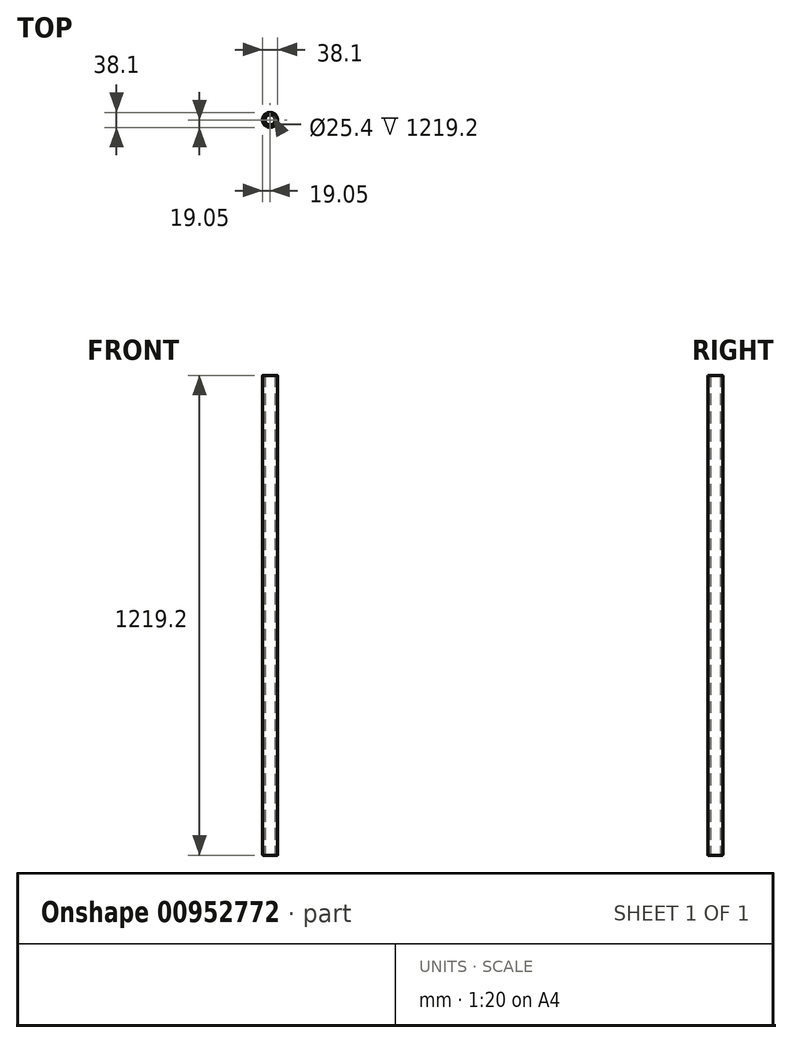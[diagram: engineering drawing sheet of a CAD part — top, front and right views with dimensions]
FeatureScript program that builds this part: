
annotation { "Feature Type Name" : "Feature", "Feature Type Description" : "" }
export const myFeature = defineFeature(function(context is Context, id is Id, definition is map)
    precondition{}
    {
        {
            var Q0;
            Q0=qCreatedBy(makeId("Top.planeOp"),FACE);
            var sketch = newSketch(context, id + "F0", { "sketchPlane" : qUnion([Q0])});
            skCircle(sketch, "E0", {"center": v(0, 0) * mm, "radius": 19.05 * mm});
            skCircle(sketch, "E1", {"center": v(0, 0) * mm, "radius": 12.7 * mm});
            skSolve(sketch);
        }
        {
            var Q0;
            Q0 = qSketchRegion(id + "F0", true);
            extrude(context, id + "F1", {"entities" : qUnion([Q0]), "endBound" : BoundingType.SYMMETRIC, "depth" : 1219.2 * mm, "offsetDistance" : 25.4 * mm});
        }
        {
            var Q0;
            Q0=makeQuery(id+"F1.opExtrude","SWEPT_FACE",FACE,{"disambiguationData":[OSD([sQuery(id+"F0.wireOp",EDGE,"E0")])]});
            fillet(context, id + "F2", {"entities" : qUnion([Q0]), "radius" : 1.27 * mm, "tangentPropagation" : true, "allowEdgeOverflow" : false});
        }
    });
